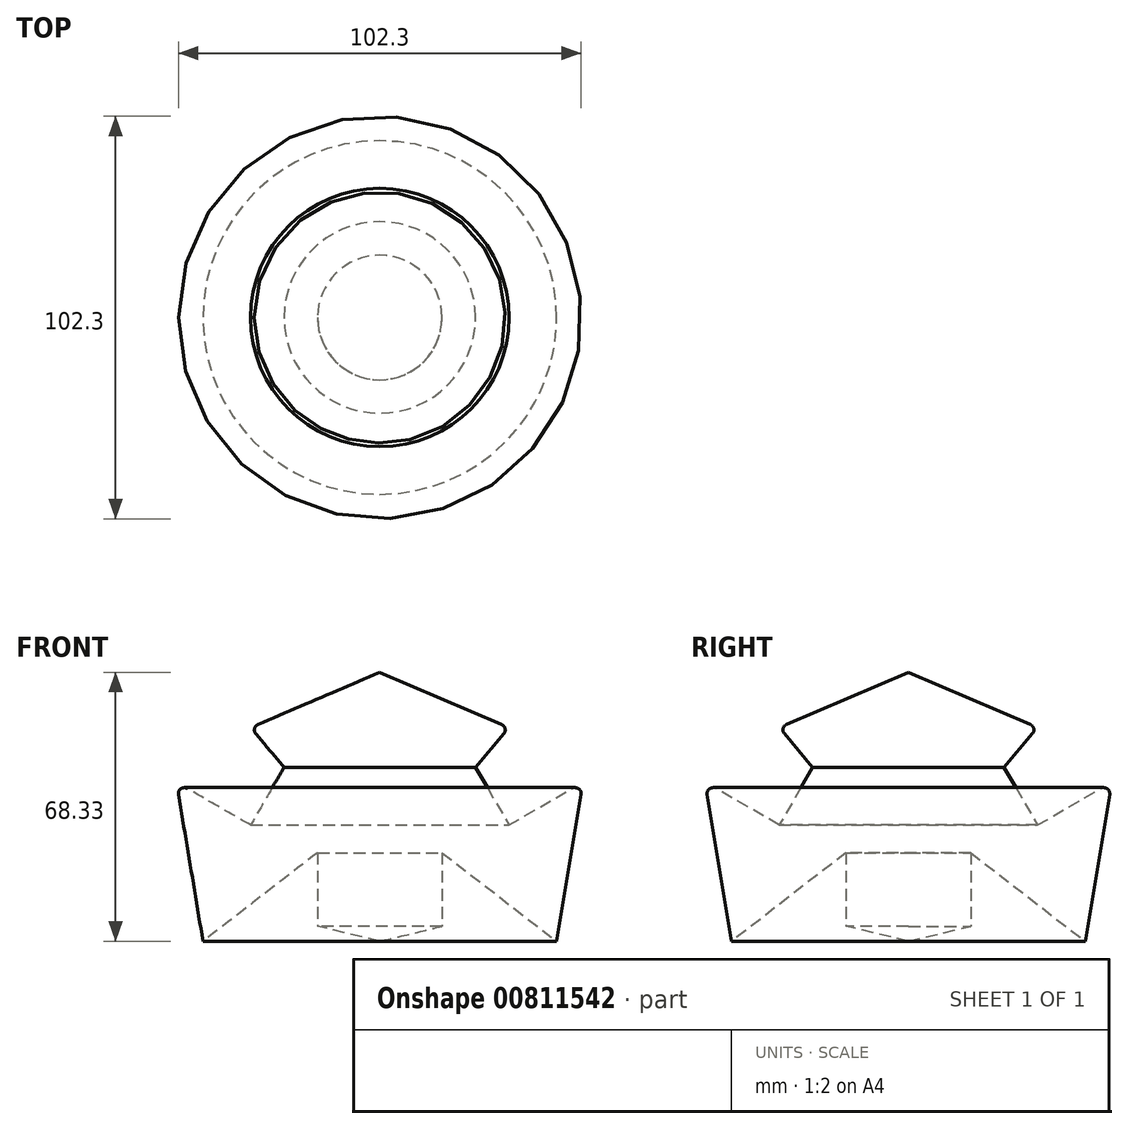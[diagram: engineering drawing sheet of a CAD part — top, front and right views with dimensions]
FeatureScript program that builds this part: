
annotation { "Feature Type Name" : "Feature", "Feature Type Description" : "" }
export const myFeature = defineFeature(function(context is Context, id is Id, definition is map)
    precondition{}
    {
        {
            var Q0;
            Q0=qCreatedBy(makeId("Front.planeOp"),FACE);
            var sketch = newSketch(context, id + "F0", { "sketchPlane" : qUnion([Q0])});
            skLineSegment(sketch, "E0", {"start": v(0, 0) * mm, "end": v(0, 68.33) * mm});
            skLineSegment(sketch, "E1", {"start": v(0, 68.33) * mm, "end": v(32.83, 54.29) * mm});
            skLineSegment(sketch, "E2", {"start": v(32.83, 54.29) * mm, "end": v(24.32, 44.22) * mm});
            skLineSegment(sketch, "E3", {"start": v(24.32, 44.22) * mm, "end": v(32.83, 29.52) * mm});
            skLineSegment(sketch, "E4", {"start": v(32.83, 29.52) * mm, "end": v(51.65, 40.42) * mm});
            skLineSegment(sketch, "E5", {"start": v(51.65, 40.42) * mm, "end": v(44.92, 0) * mm});
            skLineSegment(sketch, "E6", {"start": v(44.92, 0) * mm, "end": v(15.81, 22.51) * mm});
            skLineSegment(sketch, "E7", {"start": v(15.81, 22.51) * mm, "end": v(15.81, 3.83) * mm});
            skLineSegment(sketch, "E8", {"start": v(15.81, 3.83) * mm, "end": v(0, 0) * mm});
            skSolve(sketch);
        }
        {
            var Q0;
            Q0=makeQuery(id+"F0.imprint","IMPRINT",FACE,{"disambiguationData":[TD([[makeQuery(id+"F0.imprint","IMPRINT",EDGE,{"derivedFrom":sQuery(id+"F0.wireOp",EDGE,"E0")}),-1.0]])]});
            var Q1;
            Q1=sQuery(id+"F0.wireOp",EDGE,"E0");
            revolve(context, id + "F1", {"surfaceOperationType" : NewSurfaceOperationType.NEW, "entities" : qUnion([Q0]), "axis" : qUnion([Q1]), "revolveType" : RevolveType.FULL});
        }
        {
            var Q0;
            Q0=makeQuery(id+"F1.opRevolve","SWEPT_EDGE",EDGE,{"disambiguationData":[OSD([sQuery(id+"F0.wireOp",EDGE,"E4"),sQuery(id+"F0.wireOp",EDGE,"E5")])]});
            var Q1;
            Q1=makeQuery(id+"F1.opRevolve","SWEPT_EDGE",EDGE,{"disambiguationData":[OSD([sQuery(id+"F0.wireOp",EDGE,"E1"),sQuery(id+"F0.wireOp",EDGE,"E2")])]});
            fillet(context, id + "F2", {"entities" : qUnion([Q0, Q1]), "radius" : 1.49 * mm, "tangentPropagation" : true, "allowEdgeOverflow" : false});
        }
    });
